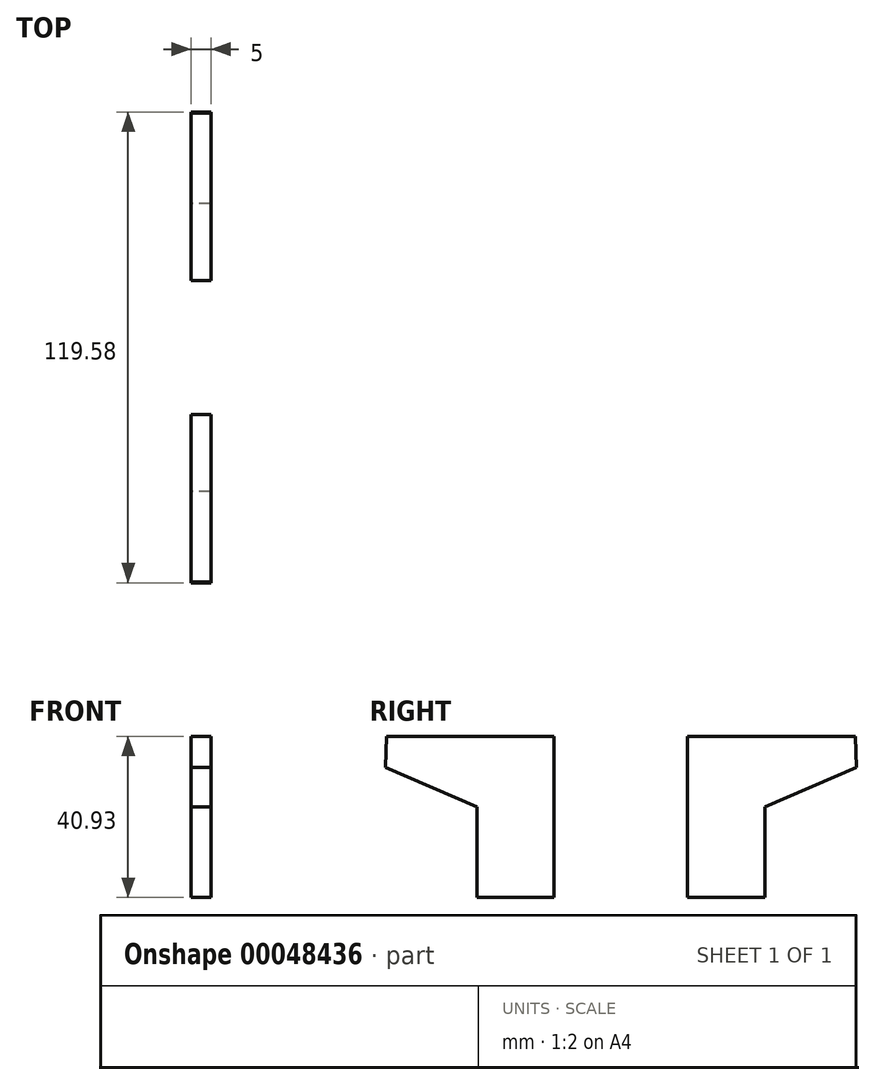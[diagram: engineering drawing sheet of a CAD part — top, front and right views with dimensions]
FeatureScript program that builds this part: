
annotation { "Feature Type Name" : "Feature", "Feature Type Description" : "" }
export const myFeature = defineFeature(function(context is Context, id is Id, definition is map)
    precondition{}
    {
        {
            var Q0;
            Q0=qCreatedBy(makeId("Right.planeOp"),FACE);
            var sketch = newSketch(context, id + "F0", { "sketchPlane" : qUnion([Q0])});
            skLineSegment(sketch, "E0", {"start": v(-59.58, 63.28) * mm, "end": v(-16.98, 63.28) * mm});
            skLineSegment(sketch, "E1", {"start": v(-16.98, 63.28) * mm, "end": v(-16.98, 22.35) * mm});
            skLineSegment(sketch, "E2", {"start": v(-16.98, 22.35) * mm, "end": v(-36.6, 22.35) * mm});
            skLineSegment(sketch, "E3", {"start": v(-36.6, 22.35) * mm, "end": v(-36.6, 45.36) * mm});
            skLineSegment(sketch, "E4", {"start": v(-36.6, 45.36) * mm, "end": v(-59.8, 55.36) * mm});
            skLineSegment(sketch, "E5", {"start": v(-59.8, 55.36) * mm, "end": v(-59.58, 63.28) * mm});
            skSolve(sketch);
        }
        {
            var Q0;
            Q0 = qSketchRegion(id + "F0", true);
            extrude(context, id + "F1", {"entities" : qUnion([Q0]), "depth" : 5 * mm});
        }
        {
            var Q0;
            Q0=makeQuery(id+"F1.opExtrude","SWEPT_BODY",BODY,{"disambiguationData":[OSD([sQuery(id+"F0.wireOp",EDGE,"E0"),sQuery(id+"F0.wireOp",EDGE,"E1"),sQuery(id+"F0.wireOp",EDGE,"E2"),sQuery(id+"F0.wireOp",EDGE,"E3"),sQuery(id+"F0.wireOp",EDGE,"E4"),sQuery(id+"F0.wireOp",EDGE,"E5")])]});
            var Q1;
            Q1=qCreatedBy(makeId("Front.planeOp"),FACE);
            mirror(context, id + "F2", {"entities" : qUnion([Q0]), "mirrorPlane" : qUnion([Q1])});
        }
    });
